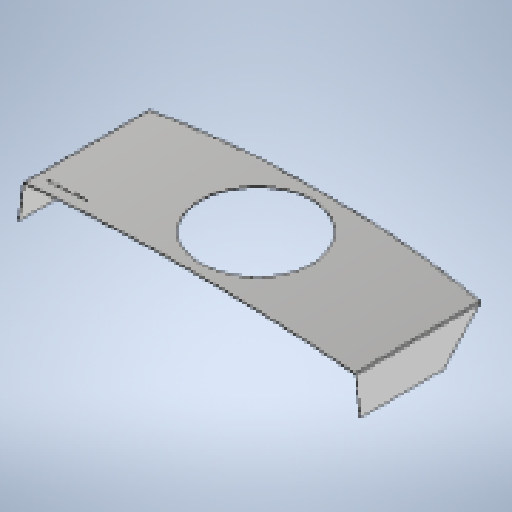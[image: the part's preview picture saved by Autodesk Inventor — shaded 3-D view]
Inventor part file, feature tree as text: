
AUTODESK INVENTOR PART (.ipt)
format: ipt  version: 2025 (Build 290162010, 162A)  size: 502,272 bytes
history: native  units: mm
features: other x4, sketch x4, sheet_metal_op x3, extrude x2
ambient origin geometry x8: Origin, YZ Plane, XZ Plane, XY Plane, X Axis, Y Axis, Z Axis, Center Point
bodies: Solid1 (feature_tree)
feature tree (13):
  sheet_metal_op  "Contour Flange1"
  other  "A-Side Definition"
  extrude  "Extrusion1"  Depth=32.0mm
  extrude  "Extrusion2"  Depth=3.0mm
  other  "Mark1"
  sketch  "Sketch1"  dims[d0=1570.0mm d1=32.0mm]
  other  "Plate1"
  sheet_metal_op  "Bend1"
  sheet_metal_op  "Corner1"
  sketch  "Sketch2"  dims[d2=40.0mm d3=3.0mm]
  sketch  "Sketch3"  dims[d4=3.0mm]
  sketch  "Sketch4"  dims[d5=1.5mm d6=6.0mm d7=3.0mm d8=580.0mm d9=3.0mm d10=0.5mm d11=12.0mm d12=3.0mm d13=3.0mm d14=3.0mm d15=157.0mm d16=17.008234mm d18=0.0mm d19=0.0mm d20=6.981317mm d21=8688.265625mm d22=500.0mm d23=3.0mm d24=0.0mm d25=300.0mm d26=12.0mm d27=200.0mm d28=50.0mm d29=50.0mm]
  other  "Definition1"
